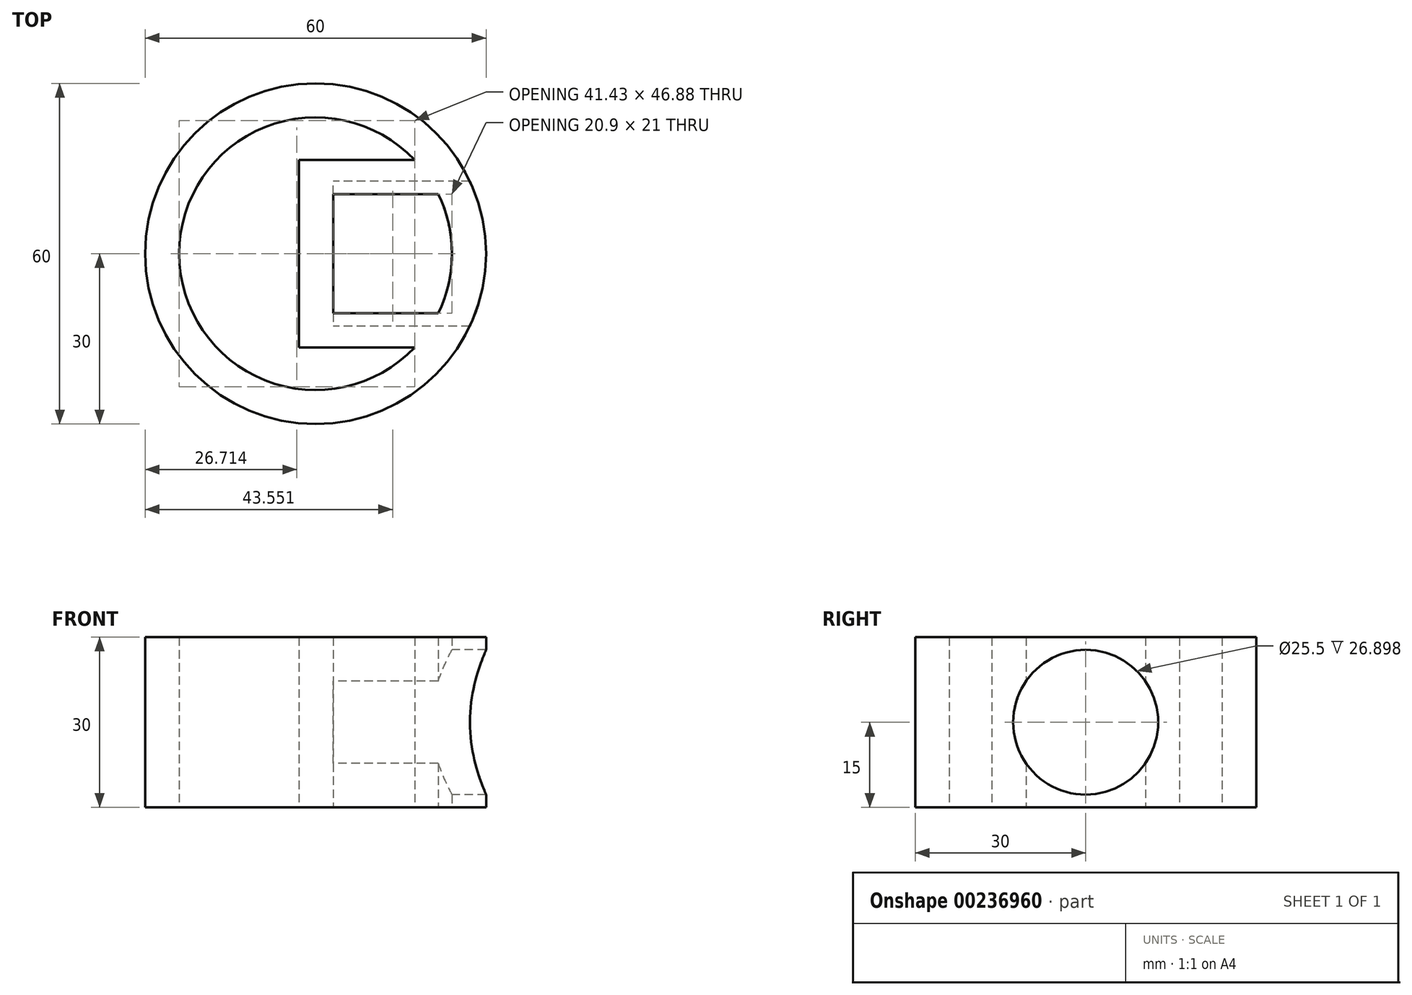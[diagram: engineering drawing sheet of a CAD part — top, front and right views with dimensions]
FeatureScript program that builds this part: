
annotation { "Feature Type Name" : "Feature", "Feature Type Description" : "" }
export const myFeature = defineFeature(function(context is Context, id is Id, definition is map)
    precondition{}
    {
        {
            var Q0;
            Q0=qCreatedBy(makeId("Top.planeOp"),FACE);
            var sketch = newSketch(context, id + "F0", { "sketchPlane" : qUnion([Q0])});
            skCircle(sketch, "E0", {"center": v(0, 0) * mm, "radius": 30 * mm});
            skCircle(sketch, "E1", {"center": v(0, 0) * mm, "radius": 24 * mm});
            skLineSegment(sketch, "E2.bottom", {"start": v(28.1, -10.5) * mm, "end": v(3.1, -10.5) * mm});
            skLineSegment(sketch, "E2.top", {"start": v(28.1, 10.5) * mm, "end": v(3.1, 10.5) * mm});
            skLineSegment(sketch, "E2.left", {"start": v(28.1, -10.5) * mm, "end": v(28.1, 10.5) * mm});
            skLineSegment(sketch, "E2.right", {"start": v(3.1, -10.5) * mm, "end": v(3.1, 10.5) * mm});
            skPoint(sketch, "E2.middle", {"position": v(15.6, 0) * mm});
            skLineSegment(sketch, "E3.0", {"start": v(28.1, -16.5) * mm, "end": v(-2.9, -16.5) * mm});
            skLineSegment(sketch, "E3.1", {"start": v(-2.9, -16.5) * mm, "end": v(-2.9, 16.5) * mm});
            skLineSegment(sketch, "E3.2", {"start": v(28.1, 16.5) * mm, "end": v(-2.9, 16.5) * mm});
            skSolve(sketch);
        }
        {
            var Q0;
            Q0=qSketchRegion(id+"F0",true);
            var Q1;
            {var subQ0=sQuery(id+"F0.wireOp",EDGE,"E2.right");Q1=makeQuery(id+"F0.imprint","IMPRINT",FACE,{"disambiguationData":[TD([[makeQuery(id+"F0.imprint","IMPRINT",EDGE,{"derivedFrom":subQ0}),1.0]])]});}
            extrude(context, id + "F1", {"entities" : qUnion([Q0, Q1]), "depth" : 30 * mm});
        }
        {
            var Q0;
            Q0=makeQuery(id+"F1.opExtrude","SWEPT_FACE",FACE,{"disambiguationData":[OSD([sQuery(id+"F0.wireOp",EDGE,"E2.right")])]});
            var sketch = newSketch(context, id + "F2", { "sketchPlane" : qUnion([Q0])});
            skCircle(sketch, "E4", {"center": v(0, 15) * mm, "radius": 12.75 * mm});
            skSolve(sketch);
        }
        {
            var Q0;
            Q0=qSketchRegion(id+"F2",true);
            extrude(context, id + "F3", {"entities" : qUnion([Q0]), "operationType" : NewBodyOperationType.REMOVE, "depth" : 30 * mm});
        }
    });
